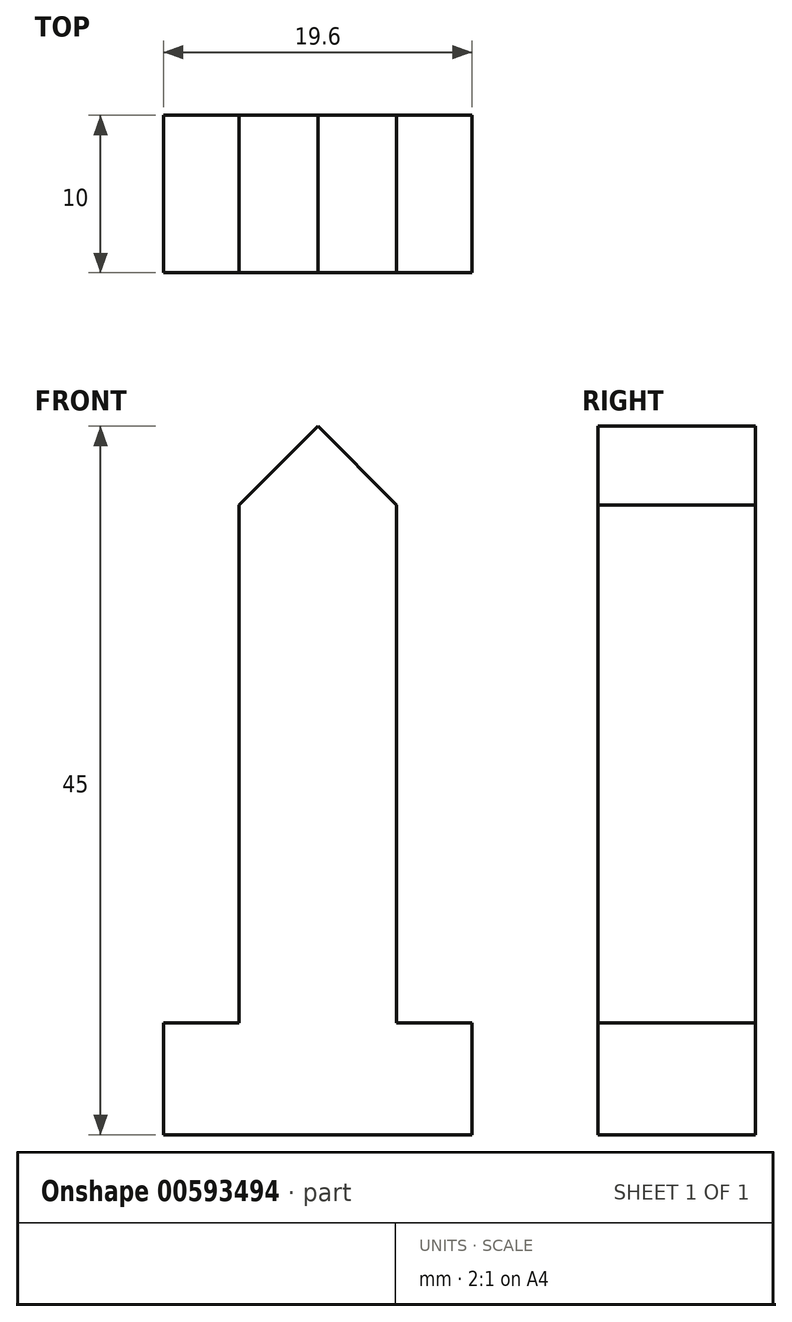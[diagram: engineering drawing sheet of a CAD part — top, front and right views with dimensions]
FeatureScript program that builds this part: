
annotation { "Feature Type Name" : "Feature", "Feature Type Description" : "" }
export const myFeature = defineFeature(function(context is Context, id is Id, definition is map)
    precondition{}
    {
        {
            var Q0;
            Q0=qCreatedBy(makeId("Front.planeOp"),FACE);
            var sketch = newSketch(context, id + "F0", { "sketchPlane" : qUnion([Q0])});
            skLineSegment(sketch, "E0", {"start": v(-9.8, 0) * mm, "end": v(-9.8, 7.1) * mm});
            skLineSegment(sketch, "E1", {"start": v(-9.8, 7.1) * mm, "end": v(-5, 7.1) * mm});
            skLineSegment(sketch, "E2", {"start": v(-5, 7.1) * mm, "end": v(-5, 40) * mm});
            skLineSegment(sketch, "E3", {"start": v(0, 45) * mm, "end": v(-5, 40) * mm});
            skLineSegment(sketch, "E4", {"start": v(5, 40) * mm, "end": v(0, 45) * mm});
            skLineSegment(sketch, "E5", {"start": v(5, 7.1) * mm, "end": v(9.8, 7.1) * mm});
            skLineSegment(sketch, "E6", {"start": v(9.8, 7.1) * mm, "end": v(9.8, 0) * mm});
            skLineSegment(sketch, "E7", {"start": v(9.8, 0) * mm, "end": v(-9.8, 0) * mm});
            skLineSegment(sketch, "E8", {"start": v(5, 40) * mm, "end": v(5, 7.1) * mm});
            skSolve(sketch);
        }
        {
            var Q0;
            Q0=makeQuery(id+"F0.imprint","IMPRINT",FACE,{"disambiguationData":[TD([[makeQuery(id+"F0.imprint","IMPRINT",EDGE,{"derivedFrom":sQuery(id+"F0.wireOp",EDGE,"E0")}),-1.0]])]});
            extrude(context, id + "F1", {"entities" : qUnion([Q0]), "depth" : 10 * mm, "offsetDistance" : 25.4 * mm});
        }
    });
